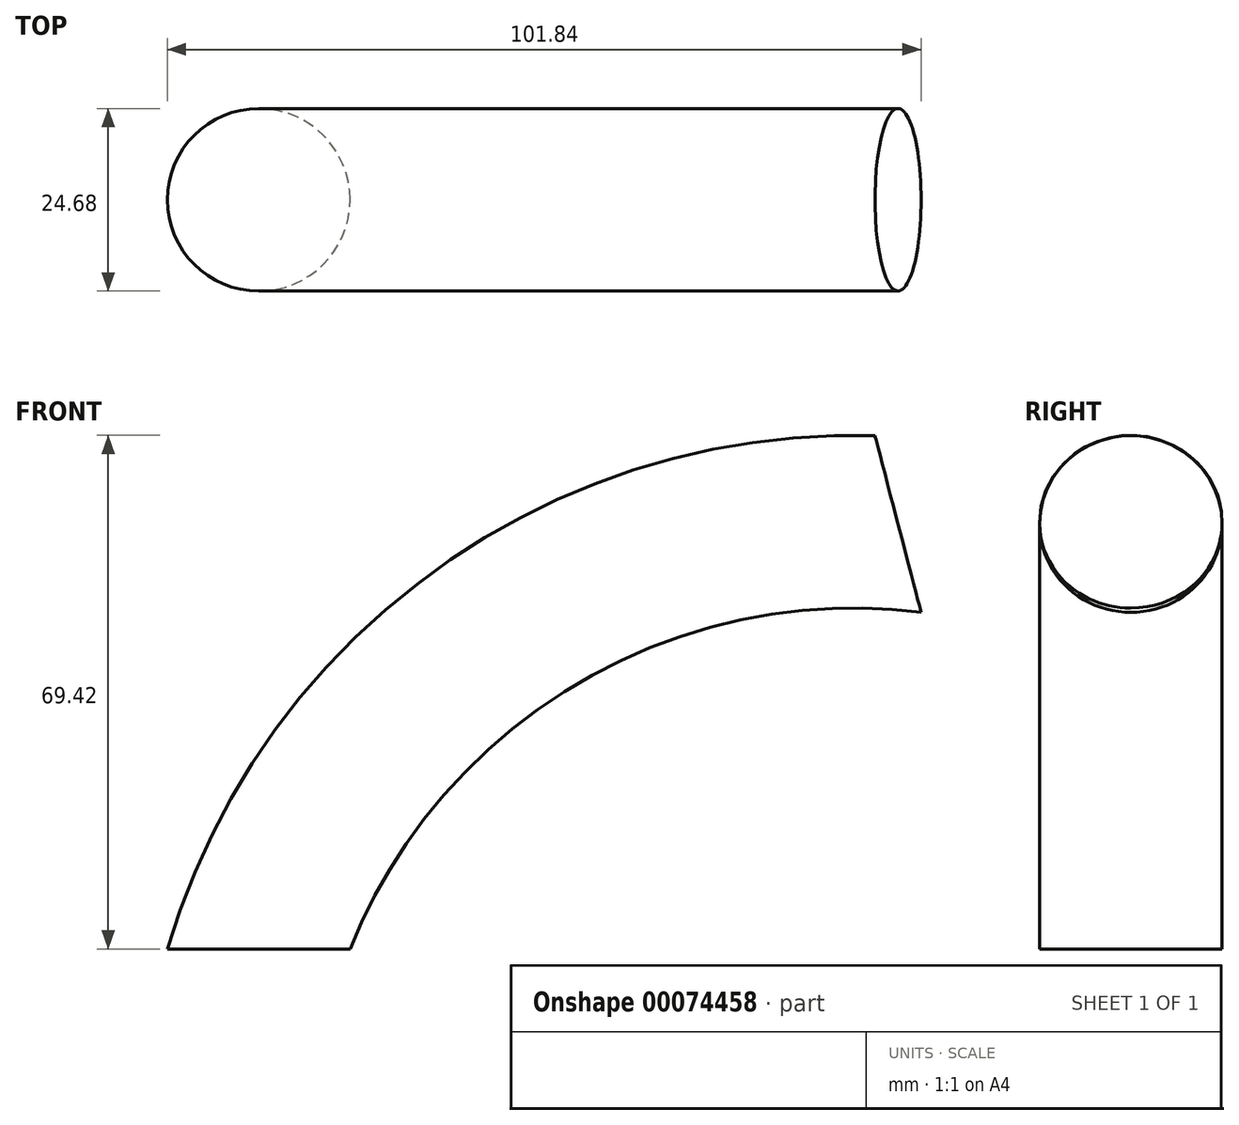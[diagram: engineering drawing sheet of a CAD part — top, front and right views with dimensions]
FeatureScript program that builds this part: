
annotation { "Feature Type Name" : "Feature", "Feature Type Description" : "" }
export const myFeature = defineFeature(function(context is Context, id is Id, definition is map)
    precondition{}
    {
        {
            var Q0;
            Q0=qCreatedBy(makeId("Top.planeOp"),FACE);
            var sketch = newSketch(context, id + "F0", { "sketchPlane" : qUnion([Q0])});
            skCircle(sketch, "E0", {"center": v(-41.84, 0) * mm, "radius": 12.34 * mm});
            skSolve(sketch);
        }
        {
            var Q0;
            Q0=qCreatedBy(makeId("Front.planeOp"),FACE);
            var sketch = newSketch(context, id + "F1", { "sketchPlane" : qUnion([Q0])});
            skArc(sketch, "E1", {"start": v(44.26, 58.51) * mm, "mid": v(-9.33, 44.14) * mm, "end": v(-42.95, 0) * mm});
            skSolve(sketch);
        }
        {
            var Q0;
            Q0=makeQuery(id+"F0.imprint","IMPRINT",FACE,{"disambiguationData":[TD([[makeQuery(id+"F0.imprint","IMPRINT",EDGE,{"derivedFrom":sQuery(id+"F0.wireOp",EDGE,"E0")}),1.0]])]});
            var Q1;
            Q1=sQuery(id+"F0.wireOp",EDGE,"E0");
            var Q2;
            Q2=sQuery(id+"F1.wireOp",EDGE,"E1");
            sweep(context, id + "F2", {"bodyType" : ToolBodyType.SURFACE, "profiles" : qUnion([Q0]), "surfaceProfiles" : qUnion([Q1]), "path" : qUnion([Q2])});
        }
    });
